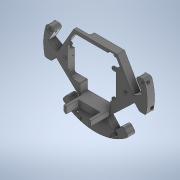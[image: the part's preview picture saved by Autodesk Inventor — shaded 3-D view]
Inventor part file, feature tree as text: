
AUTODESK INVENTOR PART (.ipt)
format: ipt  version: 2020.4 (Build 244396000, 396)  size: 997,888 bytes
history: native  units: mm
features: extrude x28, sketch x28, projected_geometry x14, plane x8, fillet x2
ambient origin geometry x8: Origin, YZ Plane, XZ Plane, XY Plane, X Axis, Y Axis, Z Axis, Center Point
bodies: Solid1 (feature_tree)
feature tree (80):
  extrude  "Extrusion1"  TaperAngle=0.0deg  [1 undecoded]
  extrude  "Extrusion2"  Depth=85.8mm
  extrude  "Extrusion3"  TaperAngle=60.0deg  [1 undecoded]
  extrude  "Extrusion4"  Depth=4.22mm
  extrude  "Extrusion5"  Depth=4.22mm
  extrude  "Extrusion6"  Depth=78.0mm
  extrude  "Extrusion7"  Depth=12.0mm
  extrude  "Extrusion8"  Depth=4.22mm
  fillet  "Fillet1"  Radius=4.22mm
  extrude  "Extrusion9"  Depth=65.0mm
  extrude  "Extrusion10"  TaperAngle=30.0deg  [1 undecoded]
  extrude  "Extrusion11"  TaperAngle=105.0deg  [1 undecoded]
  extrude  "Extrusion12"  Depth=3.0mm
  extrude  "Extrusion13"  Depth=3.0mm
  extrude  "Extrusion14"  Depth=3.0mm
  extrude  "Extrusion15"  Depth=44.0mm
  extrude  "Extrusion16"  Depth=72.0mm
  extrude  "Extrusion17"  Depth=30.0mm
  plane  "Work Plane1"
  extrude  "Extrusion18"  Depth=20.0mm
  plane  "Work Plane2"
  extrude  "Extrusion19"  Depth=3.0mm
  plane  "Work Plane3"
  extrude  "Extrusion20"  Depth=50.0mm
  plane  "Work Plane4"
  extrude  "Extrusion21"  Depth=75.0mm
  plane  "Work Plane5"
  extrude  "Extrusion22"  Depth=25.0mm
  plane  "Work Plane6"
  extrude  "Extrusion23"  Depth=10.0mm
  fillet  "Fillet3"  Radius=10.0mm
  extrude  "Extrusion30"  Depth=5.5mm
  extrude  "Extrusion31"  Depth=5.5mm
  extrude  "Extrusion32"  Depth=3.11mm
  plane  "Work Plane10"
  extrude  "Extrusion33"  Depth=3.11mm
  plane  "Work Plane11"
  extrude  "Extrusion34"  Depth=10.0mm TaperAngle=0.0deg
  sketch  "Sketch1"  dims[d0=171.6mm d1=3.0mm d2=3.0mm d3=3.0mm d4=76.0mm d5=22.0mm d6=73.0mm d7=33.2mm d8=72.0mm d9=32.0mm d10=29.0mm d11=30.0deg d12=150.0deg d13=45.0deg d14=135.0deg d15=18.0mm d16=66.0mm d17=62.0mm d18=60.0mm d19=5.0mm d20=62.240108mm d21=18.0mm d22=66.0mm d23=25.833623mm d24=52.933108mm d25=43.5mm d26=20.0mm d27=66.5mm d28=18.0mm d29=18.0mm d30=0.0mm d31=0.0mm]
  sketch  "Sketch3"  dims[d32=12.0mm d33=0.0mm d34=85.8mm]
  sketch  "Sketch4"  dims[d35=60.0deg d36=60.0deg]
  sketch  "Sketch5"  dims[d37=4.22mm d38=4.22mm]
  sketch  "Sketch6"  dims[d39=4.22mm d40=4.22mm]
  sketch  "Sketch7"  dims[d41=9.55mm d42=0.0mm d43=78.0mm]
  sketch  "Sketch8"  dims[d44=78.0mm d45=12.0mm]
  sketch  "Sketch9"  dims[d46=12.0mm d47=4.22mm d48=4.22mm]
  projected_geometry  "Projected Loop1"
  sketch  "Sketch10"  dims[d49=8.0mm d50=0.0mm d51=65.0mm]
  sketch  "Sketch11"  dims[d52=75.0deg d53=30.0deg]
  sketch  "Sketch12"  dims[d54=75.0deg d55=105.0deg]
  projected_geometry  "Projected Loop2"
  sketch  "Sketch13"  dims[d56=3.0mm d57=3.0mm]
  projected_geometry  "Projected Loop3"
  sketch  "Sketch14"  dims[d58=3.0mm d59=3.0mm]
  projected_geometry  "Projected Loop4"
  sketch  "Sketch16"  dims[d60=3.0mm d61=3.0mm]
  projected_geometry  "Projected Loop5"
  sketch  "Sketch17"  dims[d62=44.0mm d63=44.0mm]
  projected_geometry  "Projected Loop6"
  sketch  "Sketch18"  dims[d64=72.0mm d65=72.0mm]
  projected_geometry  "Projected Loop7"
  sketch  "Sketch19"  dims[d66=20.0mm d67=30.0mm]
  projected_geometry  "Projected Loop8"
  sketch  "Sketch20"  dims[d68=30.0mm d69=20.0mm]
  sketch  "Sketch21"  dims[d70=3.0mm d71=3.0mm]
  sketch  "Sketch22"  dims[d72=50.0mm d73=50.0mm]
  projected_geometry  "Projected Loop9"
  sketch  "Sketch23"  dims[d74=75.0mm d75=75.0mm]
  projected_geometry  "Projected Loop10"
  sketch  "Sketch24"  dims[d76=25.0mm d77=25.0mm]
  projected_geometry  "Projected Loop11"
  sketch  "Sketch25"  dims[d78=79.0mm d79=79.0mm d80=10.0mm d81=0.0mm]
  projected_geometry  "Projected Loop12"
  sketch  "Sketch32"  dims[d82=5.5mm d83=5.5mm]
  sketch  "Sketch33"  dims[d84=5.5mm d85=5.5mm]
  projected_geometry  "Projected Loop16"
  sketch  "Sketch34"  dims[d86=2.0mm d87=0.0mm d88=3.11mm]
  projected_geometry  "Projected Loop17"
  sketch  "Sketch35"  dims[d89=3.11mm d90=3.11mm]
  sketch  "Sketch37"  dims[d91=3.11mm d92=4.0mm d93=0.0mm d94=81.0mm d95=53.0mm d96=4.5mm d97=4.5mm d98=10.5mm d99=0.0mm d100=3.7mm d101=5.35mm d102=4.2mm d103=20.5mm d105=0.0mm d106=38.0mm d107=3.0mm d108=6.0mm d109=6.0mm d110=6.0mm d111=6.0mm d112=6.0mm d113=6.0mm d114=6.0mm d115=6.0mm d116=43.5mm d117=0.0mm d118=50.0mm d119=9.0mm d120=3.0mm d121=0.0mm d122=21.5mm d123=10.0mm d124=0.0mm d125=3.0mm d126=1.0mm d127=1.5mm d128=4.0mm d129=45.0mm d130=10.5mm d131=22.5mm d132=30.0mm d133=0.0mm d134=36.0mm d135=10.0mm d136=4.5mm d137=10.0mm d138=0.0mm d139=180.0deg d140=14.0mm d141=7.0mm d142=7.0mm d143=0.0mm d144=3.0mm d145=5.0mm d146=2.436mm d147=12.0mm d148=5.0mm d149=0.0mm d150=0.0mm d151=3.0mm d152=5.0mm d153=2.436mm d154=10.0mm d155=0.0mm d156=3.0mm d157=5.0mm d158=2.436mm d159=10.0mm d160=0.0mm d161=3.0mm d162=5.0mm d163=2.436418mm d164=12.0mm d165=5.0mm d166=0.0mm d167=0.0mm d168=3.0mm d169=3.5mm d170=2.436418mm d171=12.0mm d172=5.0mm d173=0.0mm d174=0.0mm d175=3.0mm d176=3.5mm d177=2.436418mm d178=12.0mm d179=5.0mm d180=0.0mm d181=0.0mm d182=-1.5mm d183=5.5mm d184=3.0mm d185=0.0mm d186=-1.2mm d187=5.5mm d188=3.0mm d189=0.0mm d190=-1.2mm d191=5.5mm d192=3.0mm d193=0.0mm d194=-1.2mm d195=5.5mm d196=3.0mm d197=0.0mm d198=-1.2mm d199=5.5mm d200=3.0mm d201=0.0mm d202=-1.2mm d203=5.5mm d204=3.0mm d205=0.0mm d239=1.0mm d240=3.0mm d241=10.0mm d242=0.0mm d243=6.981317mm d244=6.981317mm d245=20.0mm d247=8.290314mm d249=20.0mm d251=8.290314mm d253=3.0mm d255=2.436418mm d256=5.0mm d257=10.0mm d258=0.0mm d259=3.0mm d260=5.0mm d261=2.436418mm d262=10.0mm d263=0.0mm d264=-2.0mm d265=5.0mm d266=10.0mm d267=0.0mm d268=-2.0mm d269=5.5mm d270=10.0mm d271=0.0mm]
note: 4 required parameter values undecoded (feature->parameter linkage not recoverable at this tier; creation-order binding heuristic only, values carry confidence <= 0.55)
